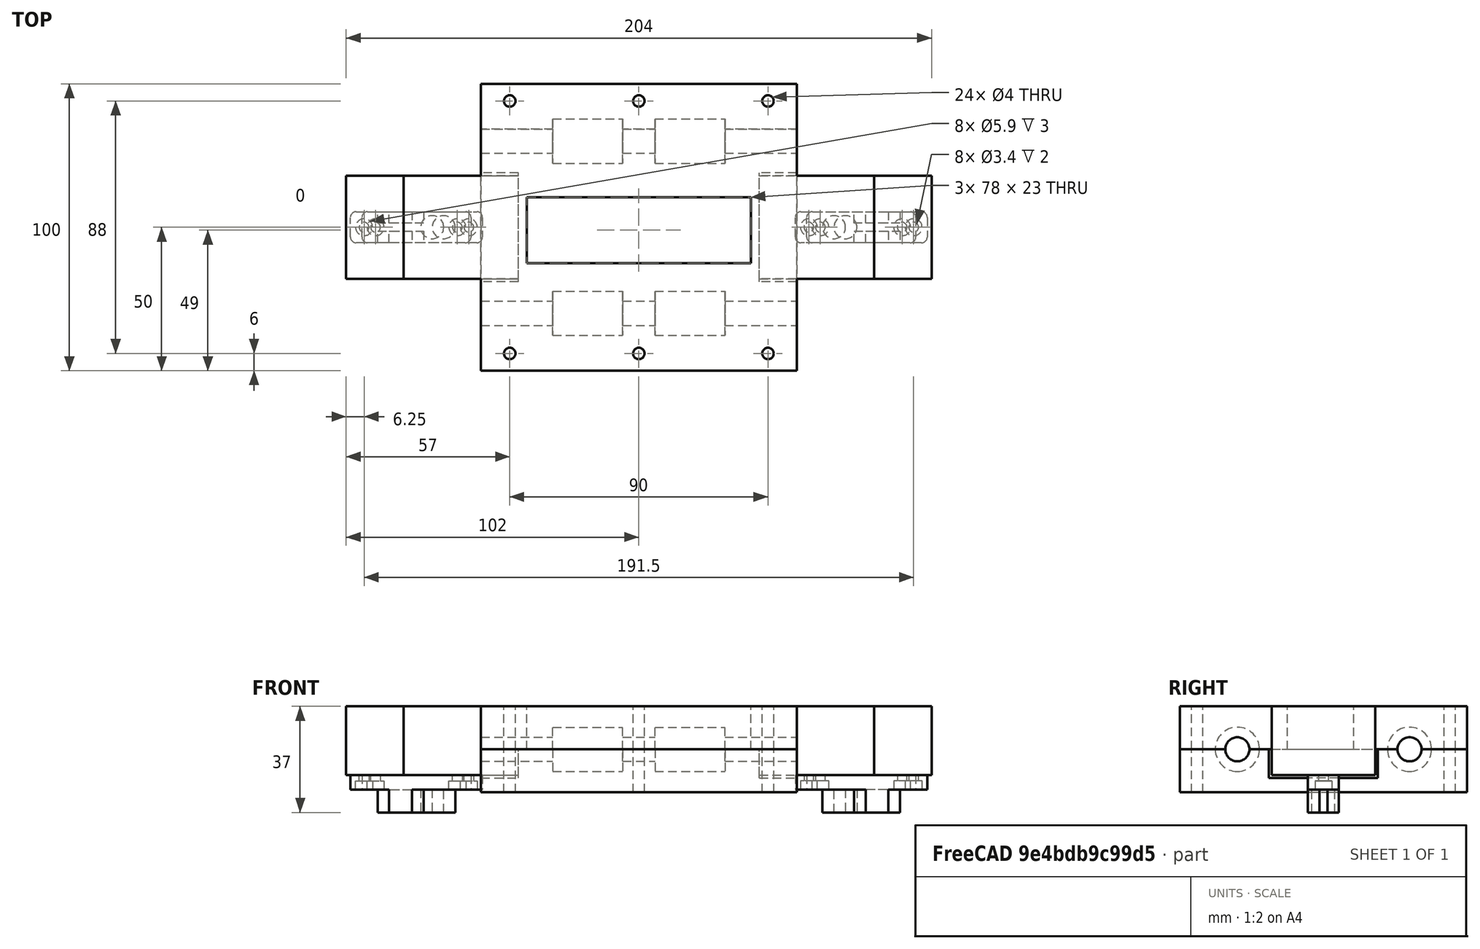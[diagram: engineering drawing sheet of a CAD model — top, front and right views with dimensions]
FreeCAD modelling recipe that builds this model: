
FCSTD DOCUMENT  (FreeCAD 0.16R6706 (Git))
Label: Soporte.bobina
License: All rights reserved
LicenseURL: http://en.wikipedia.org/wiki/All_rights_reserved
objects: Part::Cylinder×10, Part::FeaturePython×8, Part::Box×7, Part::Cut×6, Part::MultiFuse×5, Part::Fuse×4, Part::Feature×4
note: 44 computed .brp shape members not serialized (recipe doc carries the construction recipe); baked Part::Feature solids carry a one-line shape summary decoded from their .brp

FEATURE [Part::Box] Box  label="Cubo"
  Height = 15
  Length = 110
  Width = 100
FEATURE [Part::Cylinder] Cylinder  label="Eje 1"
  Angle = 360
  Height = 120
  Placement = pos=(-5,20,0) rot=(0,1,0;1.5708rad)
  Radius = 4.2
FEATURE [Part::Cylinder] Cylinder001  label="Eje 2"
  Angle = 360
  Height = 120
  Placement = pos=(-5,80,0) rot=(-0.004797,0.999977,-0.004797;1.57082rad)
  Radius = 4.2
FEATURE [Part::Cylinder] Cylinder002  label="Rodamiento 1"
  Angle = 360
  Height = 24.4
  Placement = pos=(25,20,0) rot=(0,1,0;1.5708rad)
  Radius = 7.7
FEATURE [Part::Cylinder] Cylinder005  label="Taladro tornillo"
  Angle = 360
  Height = 80
  Placement = pos=(10,6,-30) rot=(0,0,1;0rad)
  Radius = 2
FEATURE [Part::Cylinder] Cylinder004  label="Rodamiento 003"
  Angle = 360
  Height = 24.4
  Placement = pos=(25,80,0) rot=(0,1,0;1.5708rad)
  Radius = 7.7
FEATURE [Part::FeaturePython] Array001  # Draft array (typed FeaturePython)
  Angle = 360
  ArrayType = 0
  Axis = (0,0,1)
  Base = -> Cylinder002
  Center = (0,0,0)
  Fuse = false
  IntervalAxis = (0,0,0)
  IntervalX = (35.6,0,0)
  IntervalY = (0,1,0)
  IntervalZ = (0,0,0)
  NumberPolar = 1
  NumberX = 2
  NumberY = 1
  NumberZ = 1
FEATURE [Part::FeaturePython] Array  # Draft array (typed FeaturePython)
  Angle = 360
  ArrayType = 0
  Axis = (0,0,1)
  Base = -> Cylinder004
  Center = (0,0,0)
  Fuse = false
  IntervalAxis = (0,0,0)
  IntervalX = (35.6,0,0)
  IntervalY = (0,1,0)
  IntervalZ = (0,0,0)
  NumberPolar = 1
  NumberX = 2
  NumberY = 1
  NumberZ = 1
FEATURE [Part::FeaturePython] Array002  # Draft array (typed FeaturePython)
  Angle = 360
  ArrayType = 0
  Axis = (0,0,1)
  Base = -> Cylinder005
  Center = (0,0,0)
  Fuse = false
  IntervalAxis = (0,0,0)
  IntervalX = (45,0,0)
  IntervalY = (0,1,0)
  IntervalZ = (0,0,0)
  NumberPolar = 1
  NumberX = 3
  NumberY = 1
  NumberZ = 1
FEATURE [Part::Cylinder] Cylinder006  label="Taladro tornillo001"
  Angle = 360
  Height = 80
  Placement = pos=(10,6,-30) rot=(0,0,1;0rad)
  Radius = 2
FEATURE [Part::FeaturePython] Array003  # Draft array (typed FeaturePython)
  Angle = 360
  ArrayType = 0
  Axis = (0,0,1)
  Base = -> Cylinder006
  Center = (0,0,0)
  Fuse = false
  IntervalAxis = (0,0,0)
  IntervalX = (45,0,0)
  IntervalY = (0,1,0)
  IntervalZ = (0,0,0)
  NumberPolar = 1
  NumberX = 3
  NumberY = 1
  NumberZ = 1
  Placement = pos=(0,88,0) rot=(0,0,1;0rad)
FEATURE [Part::Box] Box001  label="Cubo001"
  Height = 30
  Length = 78
  Placement = pos=(16,37.5,-10) rot=(0,0,1;0rad)
  Width = 23
FEATURE [Part::Box] Box002  label="Cubo002"
  Height = 25
  Length = 40
  Placement = pos=(-27,31,-10) rot=(0,0,1;0rad)
  Width = 38
FEATURE [Part::Box] Box003  label="Cubo003"
  Height = 25
  Length = 40
  Placement = pos=(97,31,-10) rot=(0,0,1;0rad)
  Width = 38
FEATURE [Part::Box] Box004  label="Cubo004"
  Height = 15
  Length = 110
  Placement = pos=(0,0,-15) rot=(0,0,1;0rad)
  Width = 100
FEATURE [Part::MultiFuse] Fusion  label="Taladros tornillos y rodamientos"
  Shapes = -> [Array001,Array002,Array003,Array]
FEATURE [Part::MultiFuse] Fusion001  label="Ejes"
  Shapes = -> [Cylinder,Cylinder001]
FEATURE [Part::MultiFuse] Fusion002
  Shapes = -> [Box002,Box003]
FEATURE [Part::Cut] Cut  label="Parte inferior"
  Base = -> Box004
  Tool = -> Fusion002
FEATURE [Part::Box] Box006  label="Cubo006"
  Height = 24
  Length = 60
  Placement = pos=(-47,32,-9) rot=(0,0,1;0rad)
  Width = 36
FEATURE [Part::Box] Box007  label="Cubo007"
  Height = 24
  Length = 60
  Placement = pos=(97,32,-9) rot=(0,0,1;0rad)
  Width = 36
FEATURE [Part::Cut] Cut001
  Base = -> Box
  Tool = -> Box001
FEATURE [Part::MultiFuse] Fusion003
  Shapes = -> [Box006,Box007]
FEATURE [Part::Fuse] Fusion004  label="Parte superior"
  Base = -> Cut001
  Tool = -> Fusion003
FEATURE [Part::Cut] Cut002  label="Parte superior001"
  Base = -> Fusion004
  Tool = -> Fusion
FEATURE [Part::Cylinder] Cylinder007  label="Rodamiento 004"
  Angle = 360
  Height = 24.4
  Placement = pos=(25,20,0) rot=(0,1,0;1.5708rad)
  Radius = 7.7
FEATURE [Part::Cylinder] Cylinder008  label="Taladro tornillo002"
  Angle = 360
  Height = 80
  Placement = pos=(10,6,-30) rot=(0,0,1;0rad)
  Radius = 2
FEATURE [Part::Cylinder] Cylinder009  label="Rodamiento 005"
  Angle = 360
  Height = 24.4
  Placement = pos=(25,80,0) rot=(0,1,0;1.5708rad)
  Radius = 7.7
FEATURE [Part::FeaturePython] Array004  # Draft array (typed FeaturePython)
  Angle = 360
  ArrayType = 0
  Axis = (0,0,1)
  Base = -> Cylinder007
  Center = (0,0,0)
  Fuse = false
  IntervalAxis = (0,0,0)
  IntervalX = (35.6,0,0)
  IntervalY = (0,1,0)
  IntervalZ = (0,0,0)
  NumberPolar = 1
  NumberX = 2
  NumberY = 1
  NumberZ = 1
FEATURE [Part::FeaturePython] Array005  # Draft array (typed FeaturePython)
  Angle = 360
  ArrayType = 0
  Axis = (0,0,1)
  Base = -> Cylinder009
  Center = (0,0,0)
  Fuse = false
  IntervalAxis = (0,0,0)
  IntervalX = (35.6,0,0)
  IntervalY = (0,1,0)
  IntervalZ = (0,0,0)
  NumberPolar = 1
  NumberX = 2
  NumberY = 1
  NumberZ = 1
FEATURE [Part::FeaturePython] Array006  # Draft array (typed FeaturePython)
  Angle = 360
  ArrayType = 0
  Axis = (0,0,1)
  Base = -> Cylinder008
  Center = (0,0,0)
  Fuse = false
  IntervalAxis = (0,0,0)
  IntervalX = (45,0,0)
  IntervalY = (0,1,0)
  IntervalZ = (0,0,0)
  NumberPolar = 1
  NumberX = 3
  NumberY = 1
  NumberZ = 1
FEATURE [Part::Cylinder] Cylinder010  label="Taladro tornillo003"
  Angle = 360
  Height = 80
  Placement = pos=(10,6,-30) rot=(0,0,1;0rad)
  Radius = 2
FEATURE [Part::FeaturePython] Array007  # Draft array (typed FeaturePython)
  Angle = 360
  ArrayType = 0
  Axis = (0,0,1)
  Base = -> Cylinder010
  Center = (0,0,0)
  Fuse = false
  IntervalAxis = (0,0,0)
  IntervalX = (45,0,0)
  IntervalY = (0,1,0)
  IntervalZ = (0,0,0)
  NumberPolar = 1
  NumberX = 3
  NumberY = 1
  NumberZ = 1
  Placement = pos=(0,88,0) rot=(0,0,1;0rad)
FEATURE [Part::MultiFuse] Fusion005  label="Taladros tornillos y rodamientos001"
  Shapes = -> [Array004,Array006,Array007,Array005]
FEATURE [Part::Cut] Cut003  label="Parte inferior001"
  Base = -> Cut
  Tool = -> Fusion005
FEATURE [Part::Cut] Cut004
  Base = -> Cut002
  Tool = -> Fusion001
FEATURE [Part::Cut] Cut005
  Base = -> Cut003
  Tool = -> Fusion001
FEATURE [Part::Feature] belt_clamp
  Placement = pos=(-17,50,-9) rot=(0,1,0;3.14159rad)
  shape: bbox 42 x 10.8 x 14 mm, 26 faces (baked)
FEATURE [Part::Feature] Cut004002  label="Cut007"
  shape: bbox 164 x 100 x 24 mm, 48 faces (baked)
FEATURE [Part::Feature] belt_clamp001
  Placement = pos=(127,50,-9) rot=(1,0,0;3.14159rad)
  shape: bbox 42 x 10.8 x 14 mm, 26 faces (baked)
FEATURE [Part::Fuse] Fusion006
  Base = -> Cut004
  Tool = -> belt_clamp001
FEATURE [Part::Fuse] Fusion007
  Base = -> Fusion006
  Tool = -> belt_clamp
FEATURE [Part::Fuse] Fusion008
  Base = -> Fusion006
  Tool = -> belt_clamp
FEATURE [Part::Feature] Fusion008001  label="Fusion009"
  shape: bbox 204 x 100 x 37 mm, 102 faces (baked)
